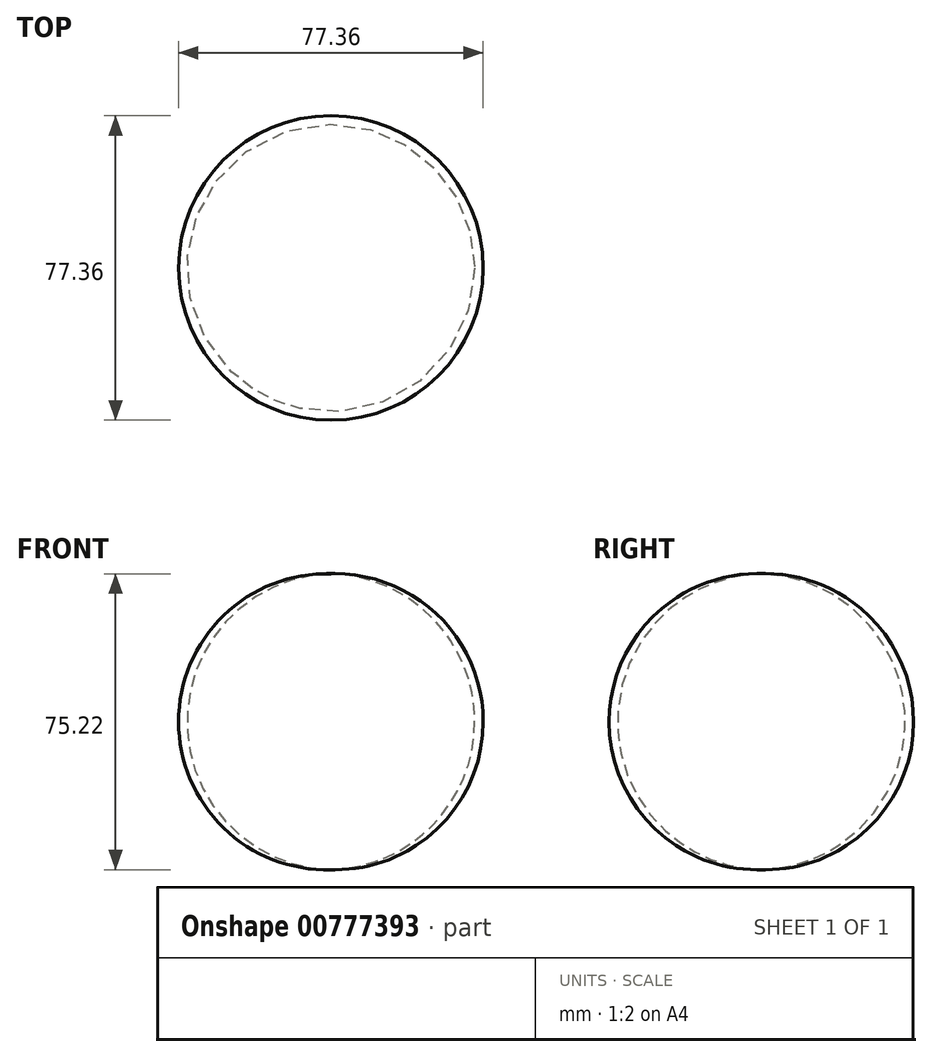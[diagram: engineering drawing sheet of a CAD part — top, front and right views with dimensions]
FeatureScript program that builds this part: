
annotation { "Feature Type Name" : "Feature", "Feature Type Description" : "" }
export const myFeature = defineFeature(function(context is Context, id is Id, definition is map)
    precondition{}
    {
        {
            var Q0;
            Q0=qCreatedBy(makeId("Front.planeOp"),FACE);
            var sketch = newSketch(context, id + "F0", { "sketchPlane" : qUnion([Q0])});
            skLineSegment(sketch, "E0", {"start": v(0, 0) * mm, "end": v(0, 75.19) * mm});
            skArc(sketch, "E1", {"start": v(0, 0) * mm, "mid": v(36.54, 37.6) * mm, "end": v(0, 75.19) * mm});
            skSolve(sketch);
        }
        {
            var Q0;
            Q0=makeQuery(id+"F0.imprint","IMPRINT",FACE,{"disambiguationData":[TD([[makeQuery(id+"F0.imprint","IMPRINT",EDGE,{"derivedFrom":sQuery(id+"F0.wireOp",EDGE,"E0")}),-1.0]])]});
            var Q1;
            Q1=sQuery(id+"F0.wireOp",EDGE,"E0");
            revolve(context, id + "F1", {"surfaceOperationType" : NewSurfaceOperationType.NEW, "entities" : qUnion([Q0]), "axis" : qUnion([Q1]), "revolveType" : RevolveType.FULL});
        }
    });
